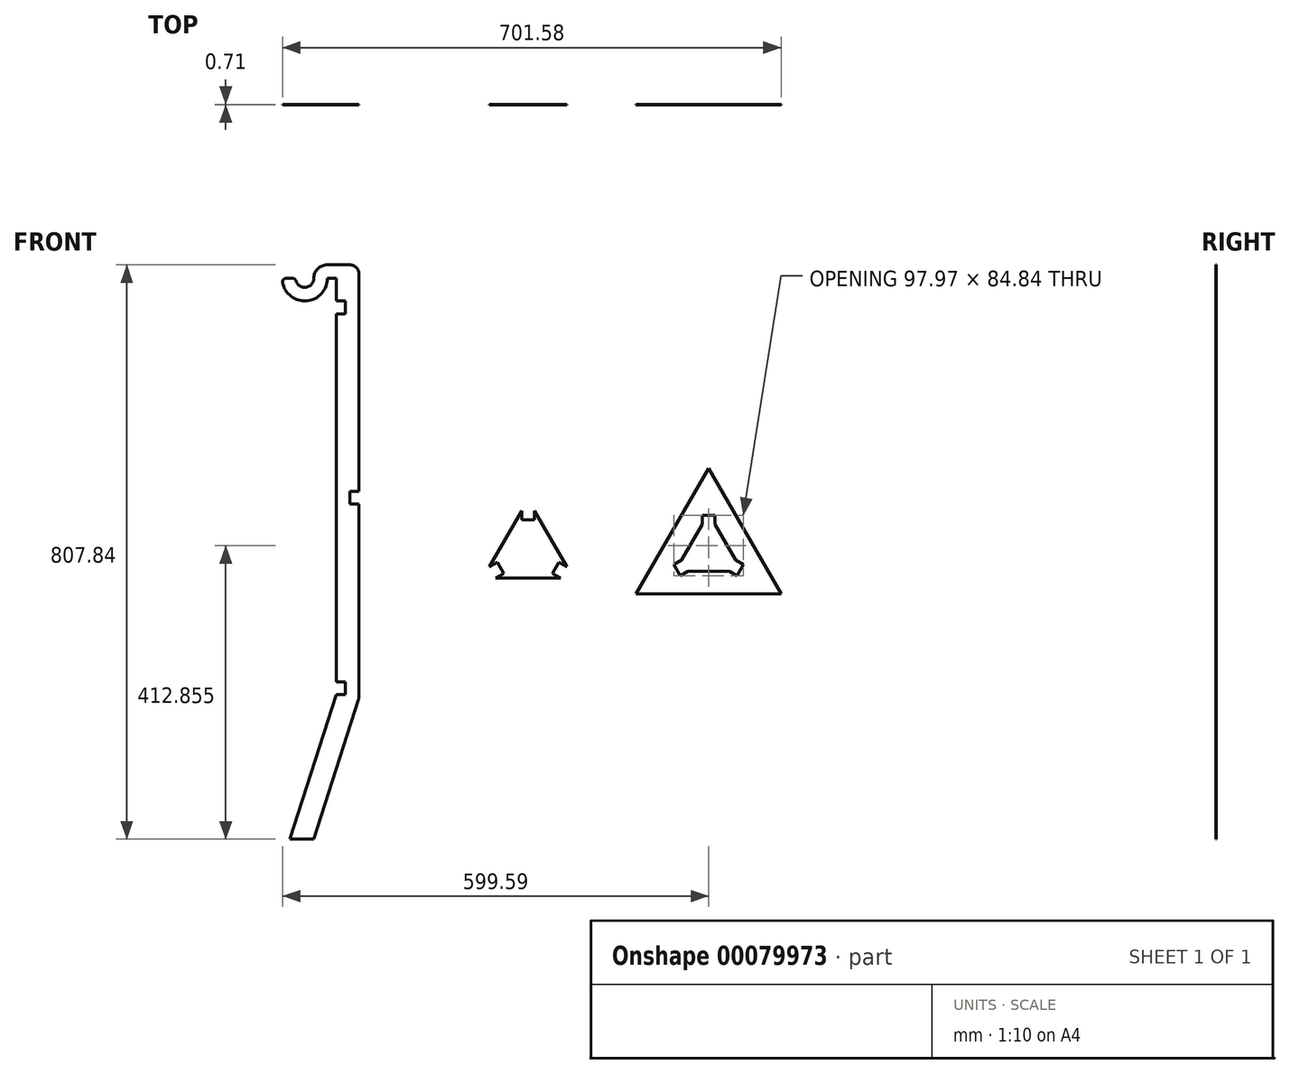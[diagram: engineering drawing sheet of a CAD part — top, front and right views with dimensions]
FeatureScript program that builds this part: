
annotation { "Feature Type Name" : "Feature", "Feature Type Description" : "" }
export const myFeature = defineFeature(function(context is Context, id is Id, definition is map)
    precondition{}
    {
        {
            assignVariable(context, id + "F0", {"name" : "Thickness", "anyValue" : .71});
        }
        {
            var Q0;
            Q0=qCreatedBy(makeId("Front.planeOp"),FACE);
            var sketch = newSketch(context, id + "F1", { "sketchPlane" : qUnion([Q0])});
            skLineSegment(sketch, "E0.bottom", {"start": v(-15.88, 403.92) * mm, "end": v(15.87, 403.92) * mm});
            skLineSegment(sketch, "E0.left", {"start": v(-15.88, 403.92) * mm, "end": v(-15.87, -200.72) * mm});
            skLineSegment(sketch, "E0.right", {"start": v(15.87, 403.92) * mm, "end": v(15.88, -205.68) * mm});
            skPoint(sketch, "E0.middle", {"position": v(0, 0) * mm});
            skLineSegment(sketch, "E1.bottom", {"start": v(-15.88, 403.92) * mm, "end": v(-28.58, 403.92) * mm});
            skLineSegment(sketch, "E1.top", {"start": v(-15.88, 384.87) * mm, "end": v(-28.58, 384.87) * mm});
            skLineSegment(sketch, "E1.left", {"start": v(-15.88, 403.92) * mm, "end": v(-15.88, 384.87) * mm});
            skLineSegment(sketch, "E2", {"start": v(-28.58, 403.92) * mm, "end": v(-28.58, 384.87) * mm});
            skArc(sketch, "E3", {"start": v(-92.08, 384.87) * mm, "mid": v(-60.33, 353.12) * mm, "end": v(-28.58, 384.87) * mm});
            skLineSegment(sketch, "E4", {"start": v(-28.58, 384.87) * mm, "end": v(-92.08, 384.87) * mm});
            skArc(sketch, "E5.0", {"start": v(-73.03, 384.87) * mm, "mid": v(-60.33, 372.17) * mm, "end": v(-47.63, 384.87) * mm});
            skArc(sketch, "E6", {"start": v(-47.63, 384.87) * mm, "mid": v(-42.05, 398.34) * mm, "end": v(-28.58, 403.92) * mm});
            skLineSegment(sketch, "E7", {"start": v(-47.62, -403.92) * mm, "end": v(15.88, -403.92) * mm});
            skLineSegment(sketch, "E8", {"start": v(-47.62, -403.92) * mm, "end": v(15.88, -205.68) * mm});
            skLineSegment(sketch, "E9.0", {"start": v(-80.96, -403.92) * mm, "end": v(-15.87, -200.72) * mm});
            skLineSegment(sketch, "E10.bottom", {"start": v(-15.87, -200.72) * mm, "end": v(-3.17, -200.72) * mm});
            skLineSegment(sketch, "E10.top", {"start": v(-15.87, -182.69) * mm, "end": v(-3.17, -182.69) * mm});
            skLineSegment(sketch, "E10.left", {"start": v(-15.87, -200.72) * mm, "end": v(-15.87, -182.69) * mm});
            skLineSegment(sketch, "E10.right", {"start": v(-3.17, -200.72) * mm, "end": v(-3.17, -182.69) * mm});
            skLineSegment(sketch, "E11.bottom", {"start": v(-15.88, 353.12) * mm, "end": v(-3.18, 353.12) * mm});
            skLineSegment(sketch, "E11.top", {"start": v(-15.88, 335.09) * mm, "end": v(-3.18, 335.09) * mm});
            skLineSegment(sketch, "E11.left", {"start": v(-15.88, 353.12) * mm, "end": v(-15.88, 335.09) * mm});
            skLineSegment(sketch, "E11.right", {"start": v(-3.17, 353.12) * mm, "end": v(-3.17, 335.09) * mm});
            skPoint(sketch, "E12", {"position": v(-60.33, 353.12) * mm});
            skLineSegment(sketch, "E13", {"start": v(-3.18, 335.09) * mm, "end": v(-3.17, -182.69) * mm, "construction": true});
            skLineSegment(sketch, "E14", {"start": v(15.87, 76.2) * mm, "end": v(-3.18, 76.2) * mm, "construction": true});
            skLineSegment(sketch, "E15.bottom", {"start": v(15.87, 76.2) * mm, "end": v(3.17, 76.2) * mm, "construction": true});
            skLineSegment(sketch, "E15.top", {"start": v(15.87, 85.22) * mm, "end": v(3.17, 85.22) * mm});
            skLineSegment(sketch, "E15.left", {"start": v(15.87, 76.2) * mm, "end": v(15.87, 85.22) * mm});
            skLineSegment(sketch, "E15.right", {"start": v(3.18, 76.2) * mm, "end": v(3.18, 85.22) * mm});
            skLineSegment(sketch, "E16.MirrorCS", {"start": v(3.18, 76.2) * mm, "end": v(3.18, 67.18) * mm});
            skLineSegment(sketch, "E17.MirrorCS", {"start": v(15.87, 67.18) * mm, "end": v(3.17, 67.18) * mm});
            skLineSegment(sketch, "E18", {"start": v(-80.96, -403.92) * mm, "end": v(-47.62, -403.92) * mm});
            skCircle(sketch, "E19.cCircle", {"center": v(254, 0) * mm, "radius": 36.66 * mm, "construction": true});
            skLineSegment(sketch, "E19.0", {"start": v(317.5, -36.66) * mm, "end": v(190.5, -36.66) * mm});
            skLineSegment(sketch, "E19.1", {"start": v(190.5, -36.66) * mm, "end": v(254, 73.32) * mm});
            skLineSegment(sketch, "E19.2", {"start": v(254, 73.32) * mm, "end": v(317.5, -36.66) * mm});
            skPoint(sketch, "E19.0.midPoint", {"position": v(254, -36.66) * mm});
            skLineSegment(sketch, "E20", {"start": v(244.98, 57.7) * mm, "end": v(263.02, 57.7) * mm});
            skLineSegment(sketch, "E21", {"start": v(244.98, 57.7) * mm, "end": v(244.98, 45) * mm});
            skLineSegment(sketch, "E22", {"start": v(244.98, 45) * mm, "end": v(263.02, 45) * mm});
            skLineSegment(sketch, "E23", {"start": v(263.02, 45) * mm, "end": v(263.02, 57.7) * mm});
            skLineSegment(sketch, "E24.1.0", {"start": v(210.52, -14.7) * mm, "end": v(199.52, -21.04) * mm});
            skLineSegment(sketch, "E24.1.1", {"start": v(219.53, -30.31) * mm, "end": v(210.52, -14.7) * mm});
            skLineSegment(sketch, "E24.1.2", {"start": v(208.53, -36.66) * mm, "end": v(219.53, -30.31) * mm});
            skLineSegment(sketch, "E24.2.0", {"start": v(288.47, -30.31) * mm, "end": v(299.47, -36.66) * mm});
            skLineSegment(sketch, "E24.2.1", {"start": v(297.48, -14.7) * mm, "end": v(288.47, -30.31) * mm});
            skLineSegment(sketch, "E24.2.2", {"start": v(308.48, -21.04) * mm, "end": v(297.48, -14.7) * mm});
            skCircle(sketch, "E25.cCircle", {"center": v(508, 0) * mm, "radius": 36.66 * mm, "construction": true});
            skLineSegment(sketch, "E25.0", {"start": v(571.5, -36.66) * mm, "end": v(444.5, -36.66) * mm, "construction": true});
            skLineSegment(sketch, "E25.1", {"start": v(444.5, -36.66) * mm, "end": v(508, 73.32) * mm, "construction": true});
            skLineSegment(sketch, "E25.2", {"start": v(508, 73.32) * mm, "end": v(571.5, -36.66) * mm, "construction": true});
            skPoint(sketch, "E25.0.midPoint", {"position": v(508, -36.66) * mm});
            skLineSegment(sketch, "E26", {"start": v(498.98, 57.7) * mm, "end": v(517.02, 57.7) * mm, "construction": true});
            skLineSegment(sketch, "E27", {"start": v(498.98, 57.7) * mm, "end": v(498.98, 45) * mm, "construction": true});
            skLineSegment(sketch, "E28", {"start": v(498.98, 45) * mm, "end": v(517.02, 45) * mm, "construction": true});
            skLineSegment(sketch, "E29", {"start": v(517.02, 45) * mm, "end": v(517.02, 57.7) * mm, "construction": true});
            skLineSegment(sketch, "E30.1.0", {"start": v(464.52, -14.7) * mm, "end": v(453.52, -21.04) * mm, "construction": true});
            skLineSegment(sketch, "E30.1.1", {"start": v(473.53, -30.31) * mm, "end": v(464.52, -14.7) * mm, "construction": true});
            skLineSegment(sketch, "E30.1.2", {"start": v(462.53, -36.66) * mm, "end": v(473.53, -30.31) * mm, "construction": true});
            skLineSegment(sketch, "E30.2.0", {"start": v(542.47, -30.31) * mm, "end": v(553.47, -36.66) * mm, "construction": true});
            skLineSegment(sketch, "E30.2.1", {"start": v(551.48, -14.7) * mm, "end": v(542.47, -30.31) * mm, "construction": true});
            skLineSegment(sketch, "E30.2.2", {"start": v(562.48, -21.04) * mm, "end": v(551.48, -14.7) * mm, "construction": true});
            skLineSegment(sketch, "E31.0", {"start": v(498.98, 38.66) * mm, "end": v(517.02, 38.66) * mm, "construction": true});
            skLineSegment(sketch, "E32", {"start": v(498.98, 38.66) * mm, "end": v(498.98, 51.36) * mm});
            skLineSegment(sketch, "E33", {"start": v(498.98, 51.36) * mm, "end": v(517.02, 51.36) * mm});
            skLineSegment(sketch, "E34", {"start": v(517.02, 51.36) * mm, "end": v(517.02, 38.66) * mm});
            skLineSegment(sketch, "E35.1.0", {"start": v(468.03, -33.49) * mm, "end": v(459.02, -17.87) * mm});
            skLineSegment(sketch, "E35.1.1", {"start": v(479.03, -27.14) * mm, "end": v(468.03, -33.49) * mm});
            skLineSegment(sketch, "E35.1.2", {"start": v(459.02, -17.87) * mm, "end": v(470.01, -11.52) * mm});
            skLineSegment(sketch, "E35.2.0", {"start": v(556.98, -17.87) * mm, "end": v(547.97, -33.49) * mm});
            skLineSegment(sketch, "E35.2.1", {"start": v(545.99, -11.52) * mm, "end": v(556.98, -17.87) * mm});
            skLineSegment(sketch, "E35.2.2", {"start": v(547.97, -33.49) * mm, "end": v(536.97, -27.14) * mm});
            skLineSegment(sketch, "E36", {"start": v(498.98, 38.66) * mm, "end": v(470.01, -11.52) * mm});
            skLineSegment(sketch, "E37", {"start": v(479.03, -27.14) * mm, "end": v(536.97, -27.14) * mm});
            skLineSegment(sketch, "E38", {"start": v(545.99, -11.52) * mm, "end": v(517.02, 38.66) * mm});
            skLineSegment(sketch, "E39.0", {"start": v(610, -58.89) * mm, "end": v(508, 117.77) * mm});
            skLineSegment(sketch, "E40.0", {"start": v(406, -58.89) * mm, "end": v(610, -58.89) * mm});
            skLineSegment(sketch, "E41.0", {"start": v(508, 117.77) * mm, "end": v(406, -58.89) * mm});
            skSolve(sketch);
        }
        {
            var Q0;
            {var subQ2=sQuery(id+"F1.wireOp",EDGE,"E0.bottom");Q0=makeQuery(id+"F1.imprint","IMPRINT",FACE,{"disambiguationData":[TD([[makeQuery(id+"F1.imprint","IMPRINT",EDGE,{"derivedFrom":subQ2}),-1.0]])]});}
            var Q1;
            {var subQ7=sQuery(id+"F1.wireOp",EDGE,"E21");Q1=makeQuery(id+"F1.imprint","IMPRINT",FACE,{"disambiguationData":[TD([[makeQuery(id+"F1.imprint","IMPRINT",EDGE,{"derivedFrom":subQ7}),-1.0]])]});}
            var Q2;
            Q2=makeQuery(id+"F1.imprint","IMPRINT",FACE,{"disambiguationData":[TD([[makeQuery(id+"F1.imprint","IMPRINT",EDGE,{"derivedFrom":sQuery(id+"F1.wireOp",EDGE,"E32")}),1.0]])]});
            var Q3;
            {var subQ0=sQuery(id+"F1.wireOp",EDGE,"E3");Q3=makeQuery(id+"F1.imprint","IMPRINT",FACE,{"disambiguationData":[TD([[makeQuery(id+"F1.imprint","IMPRINT",EDGE,{"derivedFrom":subQ0}),1.0]])]});}
            var Q4;
            {var subQ0=sQuery(id+"F1.wireOp",EDGE,"E2");Q4=makeQuery(id+"F1.imprint","IMPRINT",FACE,{"disambiguationData":[TD([[makeQuery(id+"F1.imprint","IMPRINT",EDGE,{"derivedFrom":subQ0}),-1.0]])]});}
            var Q5;
            Q5=makeQuery(id+"F1.imprint","IMPRINT",FACE,{"disambiguationData":[TD([[makeQuery(id+"F1.imprint","IMPRINT",EDGE,{"derivedFrom":sQuery(id+"F1.wireOp",EDGE,"E1.bottom")}),1.0]])]});
            extrude(context, id + "F2", {"entities" : qUnion([Q0, Q1, Q2, Q3, Q4, Q5]), "depth" : (getVariable(context, 'Thickness')) * mm});
        }
        {
            var Q0;
            Q0=makeQuery(id+"F2.opExtrude","SWEPT_EDGE",EDGE,{"disambiguationData":[OSD([sQuery(id+"F1.wireOp",EDGE,"E0.right"),sQuery(id+"F1.wireOp",EDGE,"E8")])]});
            var Q1;
            Q1=makeQuery(id+"F2.opExtrude","SWEPT_EDGE",EDGE,{"disambiguationData":[OSD([sQuery(id+"F1.wireOp",EDGE,"E0.bottom"),sQuery(id+"F1.wireOp",EDGE,"E0.right")])]});
            fillet(context, id + "F3", {"entities" : qUnion([Q0, Q1]), "radius" : 12.7 * mm, "tangentPropagation" : true, "allowEdgeOverflow" : false});
        }
        {
            var Q0;
            Q0=makeQuery(id+"F2.opExtrude","SWEPT_EDGE",EDGE,{"disambiguationData":[OSD([sQuery(id+"F1.wireOp",EDGE,"E4"),sQuery(id+"F1.wireOp",EDGE,"E5.0")])]});
            var Q1;
            Q1=makeQuery(id+"F2.opExtrude","SWEPT_EDGE",EDGE,{"disambiguationData":[OSD([sQuery(id+"F1.wireOp",EDGE,"E3"),sQuery(id+"F1.wireOp",EDGE,"E4")])]});
            fillet(context, id + "F4", {"entities" : qUnion([Q0, Q1]), "radius" : 5.08 * mm, "tangentPropagation" : true, "allowEdgeOverflow" : false});
        }
    });
